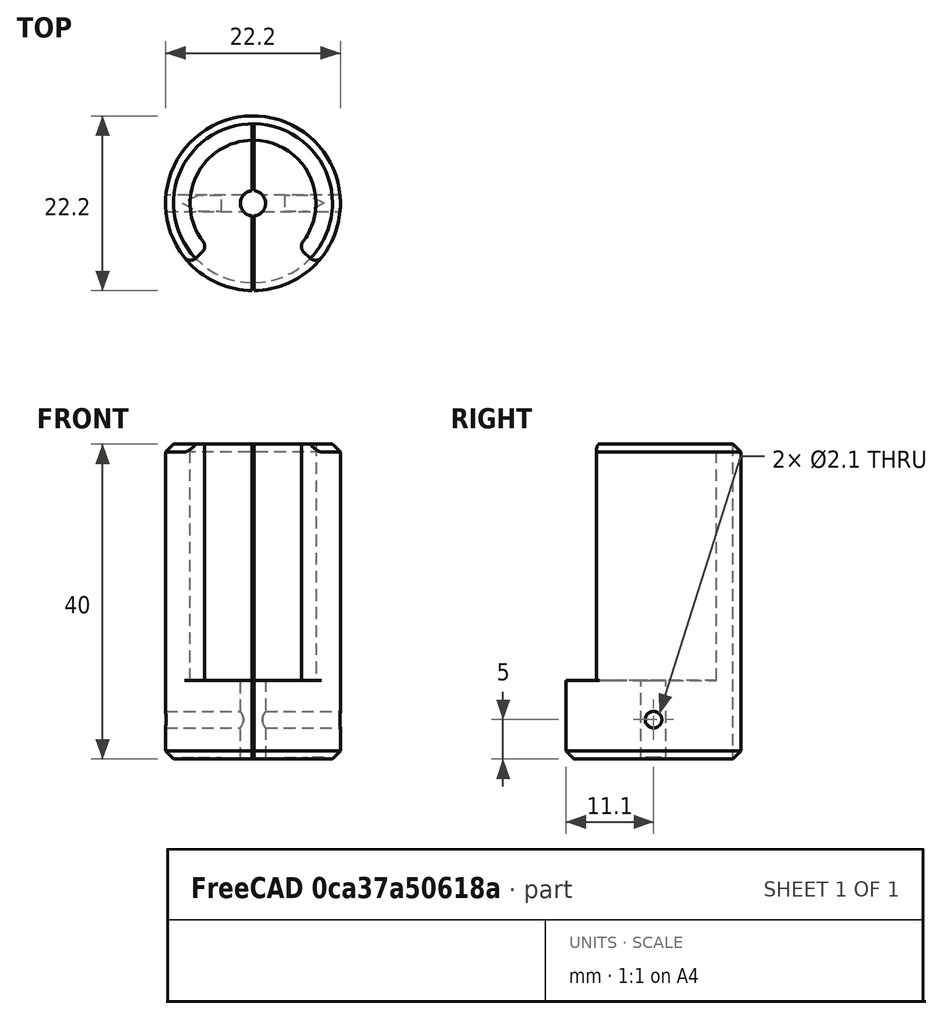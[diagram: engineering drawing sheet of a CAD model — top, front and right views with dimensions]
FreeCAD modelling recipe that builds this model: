
FCSTD DOCUMENT  (FreeCAD 0.21R33771 (Git))
Label: J-Pole_433_Base
Comment: J-Pole antenna base for BalUn ferrite
License: CC BY-SA 4.0 (SPDX-ID: CC-BY-SA-4.0)
LicenseURL: https://creativecommons.org/licenses/by-sa/4.0/legalcode.txt
objects: Sketcher::SketchObject×7, PartDesign::Pocket×6, PartDesign::Pad×1, PartDesign::Chamfer×1, PartDesign::Fillet×1, PartDesign::Body×1, Mesh::Feature×1
note: 26 computed .brp shape members not serialized (recipe doc carries the construction recipe); baked Part::Feature solids carry a one-line shape summary decoded from their .brp

FEATURE [Sketcher::SketchObject] Sketch
  FullyConstrained = true
  MapMode = 5
  Support = -> [XY_Plane]
  sketch-geometry (1):
    g0: Circle CenterX=0 CenterY=0 CenterZ=0 NormalX=0 NormalY=0 NormalZ=1 AngleXU=0 Radius=11.1
  constraints (2):
    c: Coincident(g0,g-1)
    c: Radius(g0) = 11.1
FEATURE [PartDesign::Pad] Pad
  Direction = (0,0,1)
  Length = 40
  Length2 = 10
  Profile = -> Sketch
  ReferenceAxis = -> Sketch [N_Axis]
  Type = 0
FEATURE [Sketcher::SketchObject] Sketch001
  FullyConstrained = true
  MapMode = 5
  Placement = pos=(0,0,40) rot=(0,0,1;0rad)
  Support = -> [Pad]
  sketch-geometry (1):
    g0: Circle CenterX=0 CenterY=0 CenterZ=0 NormalX=0 NormalY=0 NormalZ=1 AngleXU=0 Radius=8
  constraints (2):
    c: Coincident(g0,g-1)
    c: Radius(g0) = 8
FEATURE [PartDesign::Pocket] Pocket
  BaseFeature = -> Pad
  Direction = (0,0,-1)
  Length = 30
  Length2 = 5
  Profile = -> Sketch001
  ReferenceAxis = -> Sketch001 [N_Axis]
  Type = 0
FEATURE [Sketcher::SketchObject] Sketch002
  ExternalGeometry = -> [Pocket]
  FullyConstrained = true
  MapMode = 5
  Placement = pos=(0,0,40) rot=(0,0,1;0rad)
  Support = -> [Pocket]
  sketch-geometry (4):
    g0: LineSegment StartX=0 StartY=0 StartZ=0 EndX=-8 EndY=-7.6948 EndZ=0
    g1: LineSegment StartX=0 StartY=0 StartZ=0 EndX=8 EndY=-7.6948 EndZ=0
    g2: LineSegment StartX=-8 StartY=-7.6948 StartZ=0 EndX=8 EndY=-7.6948 EndZ=0
    g3: ArcOfCircle CenterX=0 CenterY=0 CenterZ=0 NormalX=0 NormalY=0 NormalZ=1 AngleXU=0 Radius=11.1 StartAngle=3.90755 EndAngle=5.51723
  constraints (10):
    c: Coincident(g0,g-3)
    c: PointOnObject(g0,g-3)
    c: Coincident(g1,g0)
    c: Coincident(g2,g0)
    c: Coincident(g2,g1)
    c: Horizontal(g2)
    c: Coincident(g3,g0)
    c: Coincident(g3,g0)
    c: Coincident(g3,g1)
    c: DistanceX(g2,g2) = 16
FEATURE [PartDesign::Pocket] Pocket001
  BaseFeature = -> Pocket
  Direction = (0,0,-1)
  Length = 30
  Length2 = 5
  Profile = -> Sketch002
  ReferenceAxis = -> Sketch002 [N_Axis]
  Type = 0
FEATURE [Sketcher::SketchObject] Sketch003
  FullyConstrained = true
  MapMode = 5
  Placement = pos=(0,0,10) rot=(0,0,1;0rad)
  Support = -> [Pocket001]
  sketch-geometry (1):
    g0: Circle CenterX=0 CenterY=0 CenterZ=0 NormalX=0 NormalY=0 NormalZ=1 AngleXU=0 Radius=1.6
  constraints (2):
    c: Coincident(g0,g-1)
    c: Radius(g0) = 1.6
FEATURE [PartDesign::Pocket] Pocket002
  BaseFeature = -> Pocket001
  Direction = (0,0,-1)
  Length = 5
  Length2 = 5
  Profile = -> Sketch003
  ReferenceAxis = -> Sketch003 [N_Axis]
  Type = 1
FEATURE [Sketcher::SketchObject] Sketch004
  FullyConstrained = true
  MapMode = 5
  Placement = pos=(0,0,40) rot=(0,0,1;0rad)
  Support = -> [Pocket002]
  sketch-geometry (4):
    g0: LineSegment StartX=-0.1 StartY=10 StartZ=0 EndX=0.1 EndY=10 EndZ=0
    g1: LineSegment StartX=0.1 StartY=10 StartZ=0 EndX=0.1 EndY=-12 EndZ=0
    g2: LineSegment StartX=0.1 StartY=-12 StartZ=0 EndX=-0.1 EndY=-12 EndZ=0
    g3: LineSegment StartX=-0.1 StartY=-12 StartZ=0 EndX=-0.1 EndY=10 EndZ=0
  constraints (12):
    c: Coincident(g0,g1)
    c: Coincident(g1,g2)
    c: Coincident(g2,g3)
    c: Coincident(g3,g0)
    c: Horizontal(g0)
    c: Horizontal(g2)
    c: Vertical(g1)
    c: Vertical(g3)
    c: DistanceX(g0,g0) = 0.2
    c: DistanceY(g1,g1) = 22
    c: Distance(g-1,g1) = 0.1
    c: Distance(g-1,g0) = 10
FEATURE [PartDesign::Pocket] Pocket003
  BaseFeature = -> Pocket002
  Direction = (0,0,-1)
  Length = 5
  Length2 = 5
  Profile = -> Sketch004
  ReferenceAxis = -> Sketch004 [N_Axis]
  Type = 1
FEATURE [Sketcher::SketchObject] Sketch005
  FullyConstrained = true
  MapMode = 5
  Placement = pos=(0,0,0) rot=(1,0,0;3.14159rad)
  Support = -> [Pocket003]
  sketch-geometry (10):
    g0: LineSegment StartX=4 StartY=1 StartZ=0 EndX=7 EndY=1 EndZ=0
    g1: LineSegment StartX=9 StartY=0 StartZ=0 EndX=7 EndY=1 EndZ=0
    g2: LineSegment StartX=9 StartY=0 StartZ=0 EndX=7 EndY=-1 EndZ=0
    g3: LineSegment StartX=7 StartY=-1 StartZ=0 EndX=4 EndY=-1 EndZ=0
    g4: LineSegment StartX=4 StartY=-1 StartZ=0 EndX=4 EndY=1 EndZ=0
    g5: LineSegment StartX=-9 StartY=0 StartZ=0 EndX=-7 EndY=1 EndZ=0
    g6: LineSegment StartX=-7 StartY=1 StartZ=0 EndX=-4 EndY=1 EndZ=0
    g7: LineSegment StartX=-4 StartY=1 StartZ=0 EndX=-4 EndY=-1 EndZ=0
    g8: LineSegment StartX=-4 StartY=-1 StartZ=0 EndX=-7 EndY=-1 EndZ=0
    g9: LineSegment StartX=-7 StartY=-1 StartZ=0 EndX=-9 EndY=0 EndZ=0
  constraints (30):
    c: Horizontal(g0)
    c: PointOnObject(g1,g-1)
    c: Coincident(g1,g0)
    c: Coincident(g2,g1)
    c: Coincident(g3,g2)
    c: Coincident(g4,g3)
    c: Coincident(g4,g0)
    c: Vertical(g4)
    c: Horizontal(g3)
    c: DistanceY(g4,g4) = 2
    c: Distance(g1,g4) = 5
    c: DistanceX(g0,g0) = 3
    c: DistanceX(g3,g3) = 3
    c: Distance(g-1,g4) = 4
    c: PointOnObject(g5,g-1)
    c: Coincident(g6,g5)
    c: Horizontal(g6)
    c: Coincident(g7,g6)
    c: Vertical(g7)
    c: Coincident(g8,g7)
    c: Horizontal(g8)
    c: Coincident(g9,g8)
    c: Coincident(g9,g5)
    c: DistanceY(g-1,g0) = 1
    c: DistanceY(g7,g7) = 2
    c: DistanceY(g-1,g5) = 1
    c: DistanceX(g6,g6) = 3
    c: DistanceX(g8,g8) = 3
    c: Distance(g5,g7) = 5
    c: Distance(g-1,g7) = 4
FEATURE [PartDesign::Pocket] Pocket004
  BaseFeature = -> Pocket003
  Direction = (0,0,1)
  Length = 0.2
  Length2 = 5
  Profile = -> Sketch005
  ReferenceAxis = -> Sketch005 [N_Axis]
  Type = 0
FEATURE [Sketcher::SketchObject] Sketch006
  AttachmentOffset = pos=(0,0,11.2) rot=(0,0,1;0rad)
  FullyConstrained = true
  MapMode = 5
  Placement = pos=(11.2,-2.5e-15,2.5e-15) rot=(0.57735,0.57735,0.57735;2.0944rad)
  Support = -> [YZ_Plane]
  sketch-geometry (1):
    g0: Circle CenterX=0 CenterY=5 CenterZ=0 NormalX=0 NormalY=0 NormalZ=1 AngleXU=0 Radius=1.05
  constraints (3):
    c: PointOnObject(g0,g-2)
    c: Radius(g0) = 1.05
    c: DistanceY(g-1,g0) = 5
FEATURE [PartDesign::Pocket] Pocket005
  BaseFeature = -> Pocket004
  Direction = (-1,2e-16,-3e-16)
  Length = 5
  Length2 = 5
  Profile = -> Sketch006
  ReferenceAxis = -> Sketch006 [N_Axis]
  Type = 1
FEATURE [PartDesign::Chamfer] Chamfer
  Angle = 45
  Base = -> Pocket005 [Edge1,Edge17,Edge5,Edge25]
  BaseFeature = -> Pocket005
  ChamferType = 0
  FlipDirection = false
  Size = 1
  Size2 = 1
  SupportTransform = false
  UseAllEdges = false
FEATURE [PartDesign::Fillet] Fillet
  Base = -> Chamfer [Edge20,Edge56,Edge11,Edge1]
  BaseFeature = -> Chamfer
  Radius = 1
  SupportTransform = false
  UseAllEdges = false
FEATURE [PartDesign::Body] Body
  Group = -> [Sketch,Pad,Sketch001,Pocket,Sketch002,Pocket001,Sketch003,Pocket002,Sketch004,Pocket003,Sketch005,Pocket004,Sketch006,Pocket005,Chamfer,Fillet]
  Origin = -> Origin
  Tip = -> Fillet
FEATURE [Mesh::Feature] Mesh  label="J-Pole_433_Base"
